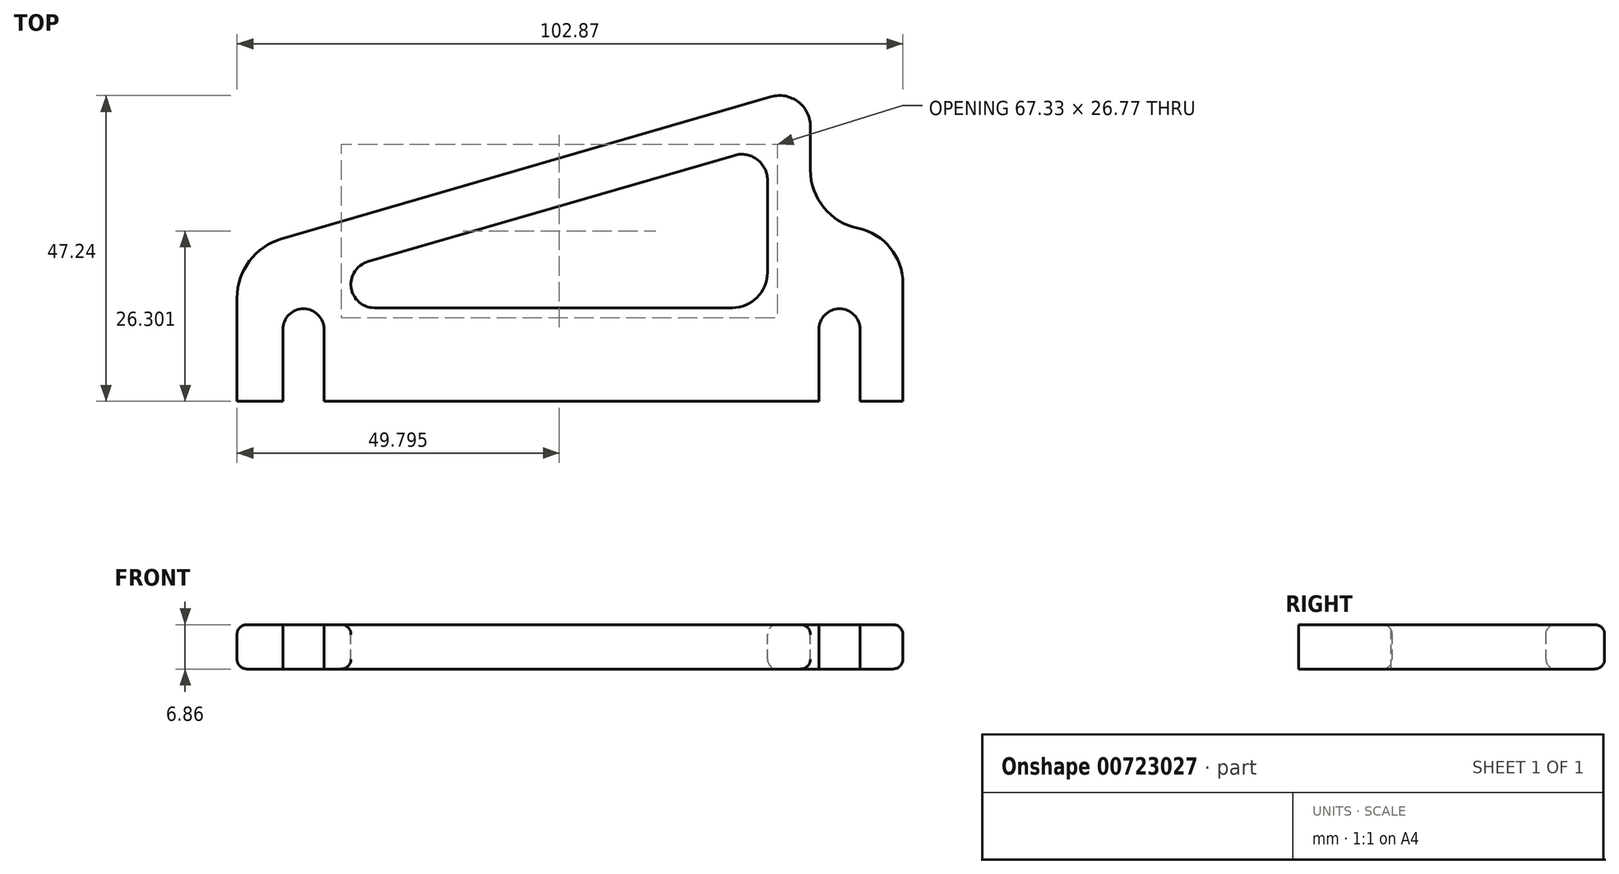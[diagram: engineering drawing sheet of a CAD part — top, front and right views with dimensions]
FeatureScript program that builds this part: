
annotation { "Feature Type Name" : "Feature", "Feature Type Description" : "" }
export const myFeature = defineFeature(function(context is Context, id is Id, definition is map)
    precondition{}
    {
        {
            var Q0;
            Q0=qCreatedBy(makeId("Top.planeOp"),FACE);
            var sketch = newSketch(context, id + "F0", { "sketchPlane" : qUnion([Q0])});
            skLineSegment(sketch, "E0", {"start": v(-39.81, 13.22) * mm, "end": v(35.81, 35.17) * mm});
            skLineSegment(sketch, "E1", {"start": v(56.19, 6.35) * mm, "end": v(56.19, -11.88) * mm});
            skLineSegment(sketch, "E2", {"start": v(56.19, -11.88) * mm, "end": v(49.57, -11.88) * mm});
            skLineSegment(sketch, "E3", {"start": v(-46.68, -11.88) * mm, "end": v(-46.68, 4.07) * mm});
            skPoint(sketch, "E4.visualSharp", {"position": v(-46.68, 11.23) * mm});
            skArc(sketch, "E4.filletArc", {"start": v(-39.81, 13.22) * mm, "mid": v(-44.77, 9.8) * mm, "end": v(-46.68, 4.07) * mm});
            skArc(sketch, "E5.filletArc", {"start": v(41.9, 30.58) * mm, "mid": v(40, 34.4) * mm, "end": v(35.81, 35.17) * mm});
            skLineSegment(sketch, "E6.0", {"start": v(-33.25, -11.88) * mm, "end": v(-33.25, -0.77) * mm});
            skLineSegment(sketch, "E7.0", {"start": v(-39.6, -11.88) * mm, "end": v(-39.6, -0.77) * mm});
            skLineSegment(sketch, "E8.0", {"start": v(43.22, -0.77) * mm, "end": v(43.22, -11.88) * mm});
            skLineSegment(sketch, "E9.0", {"start": v(49.57, -0.77) * mm, "end": v(49.57, -11.88) * mm});
            skArc(sketch, "E10", {"start": v(-39.6, -0.77) * mm, "mid": v(-36.42, 2.4) * mm, "end": v(-33.25, -0.77) * mm});
            skArc(sketch, "E11", {"start": v(43.22, -0.77) * mm, "mid": v(46.4, 2.4) * mm, "end": v(49.57, -0.77) * mm});
            skLineSegment(sketch, "E12.trimOffspring", {"start": v(-39.6, -11.88) * mm, "end": v(-46.68, -11.88) * mm});
            skLineSegment(sketch, "E13.trimOffspring", {"start": v(43.22, -11.88) * mm, "end": v(-33.25, -11.88) * mm});
            skLineSegment(sketch, "E14.0", {"start": v(-26.46, 9.7) * mm, "end": v(30.17, 26.13) * mm});
            skLineSegment(sketch, "E15", {"start": v(29.8, 2.56) * mm, "end": v(-25.44, 2.56) * mm});
            skLineSegment(sketch, "E16", {"start": v(35.26, 22.3) * mm, "end": v(35.26, 8.03) * mm});
            skPoint(sketch, "E16.endSnap0", {"position": v(-36.42, 2.4) * mm});
            skArc(sketch, "E17", {"start": v(-25.44, 2.56) * mm, "mid": v(-29.04, 5.69) * mm, "end": v(-26.46, 9.7) * mm});
            skArc(sketch, "E18", {"start": v(29.8, 2.56) * mm, "mid": v(33.66, 4.16) * mm, "end": v(35.26, 8.03) * mm});
            skArc(sketch, "E19", {"start": v(35.26, 22.3) * mm, "mid": v(33.67, 25.49) * mm, "end": v(30.17, 26.13) * mm});
            skLineSegment(sketch, "E20", {"start": v(41.9, 30.58) * mm, "end": v(41.9, 23.85) * mm});
            skArc(sketch, "E21", {"start": v(41.9, 23.85) * mm, "mid": v(43.97, 18.04) * mm, "end": v(49.25, 14.85) * mm});
            skArc(sketch, "E22", {"start": v(49.25, 14.85) * mm, "mid": v(54.23, 11.83) * mm, "end": v(56.19, 6.35) * mm});
            skSolve(sketch);
        }
        {
            var Q0;
            Q0=makeQuery(id+"F0.imprint","IMPRINT",FACE,{"disambiguationData":[TD([[makeQuery(id+"F0.imprint","IMPRINT",EDGE,{"derivedFrom":sQuery(id+"F0.wireOp",EDGE,"E0")}),-1.0]])]});
            extrude(context, id + "F1", {"entities" : qUnion([Q0]), "oppositeDirection" : true, "depth" : 6.86 * mm, "offsetDistance" : 25.4 * mm});
        }
        {
            var Q0;
            Q0=makeQuery(id+"F1.opExtrude","CAP_EDGE",EDGE,{"disambiguationData":[OSD([sQuery(id+"F0.wireOp",EDGE,"E0")])],"isStart":true});
            var Q1;
            Q1=makeQuery(id+"F1.opExtrude","CAP_EDGE",EDGE,{"disambiguationData":[OSD([sQuery(id+"F0.wireOp",EDGE,"E22")])],"isStart":true});
            var Q2;
            Q2=makeQuery(id+"F1.opExtrude","CAP_EDGE",EDGE,{"disambiguationData":[OSD([sQuery(id+"F0.wireOp",EDGE,"E14.0")])],"isStart":true});
            fillet(context, id + "F2", {"entities" : qUnion([Q0, Q1, Q2]), "radius" : 1.52 * mm, "tangentPropagation" : true, "allowEdgeOverflow" : false});
        }
        {
            var Q0;
            Q0=makeQuery(id+"F1.opExtrude","CAP_EDGE",EDGE,{"disambiguationData":[OSD([sQuery(id+"F0.wireOp",EDGE,"E0")])],"isStart":false});
            var Q1;
            Q1=makeQuery(id+"F1.opExtrude","CAP_EDGE",EDGE,{"disambiguationData":[OSD([sQuery(id+"F0.wireOp",EDGE,"E20")])],"isStart":false});
            fillet(context, id + "F3", {"entities" : qUnion([Q0, Q1]), "radius" : 1.52 * mm, "tangentPropagation" : true, "allowEdgeOverflow" : false});
        }
        {
            var Q0;
            Q0=makeQuery(id+"F1.opExtrude","CAP_EDGE",EDGE,{"disambiguationData":[OSD([sQuery(id+"F0.wireOp",EDGE,"E15")])],"isStart":false});
            fillet(context, id + "F4", {"entities" : qUnion([Q0]), "radius" : 1.52 * mm, "tangentPropagation" : true, "allowEdgeOverflow" : false});
        }
    });
